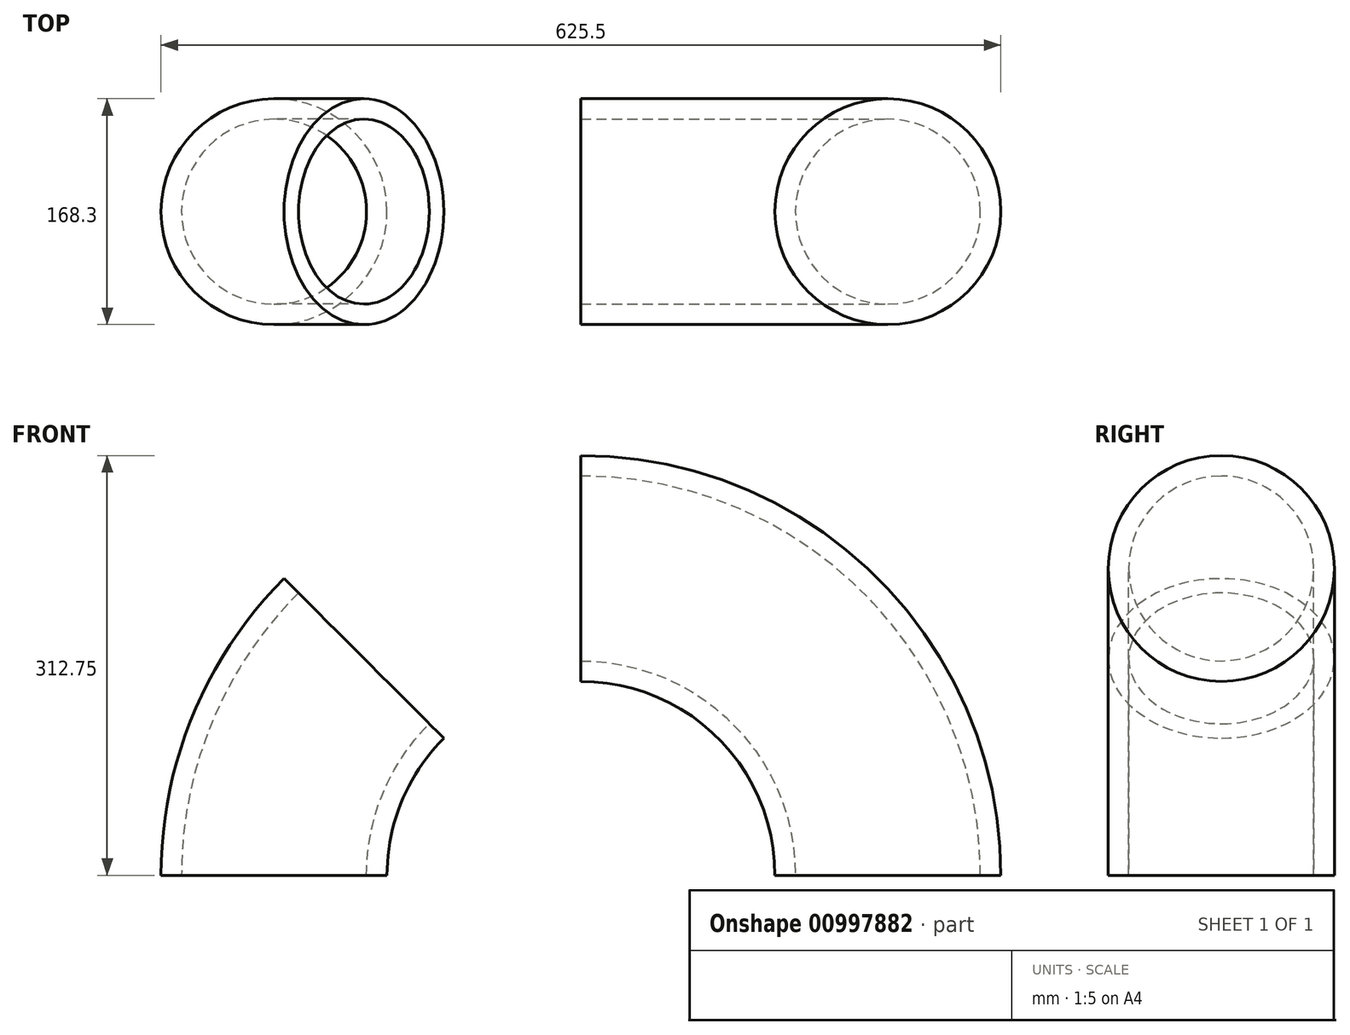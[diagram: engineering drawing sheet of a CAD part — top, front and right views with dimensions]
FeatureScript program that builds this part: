
annotation { "Feature Type Name" : "Feature", "Feature Type Description" : "" }
export const myFeature = defineFeature(function(context is Context, id is Id, definition is map)
    precondition{}
    {
        {
            var Q0;
            Q0=qCreatedBy(makeId("Front.planeOp"),FACE);
            var sketch = newSketch(context, id + "F0", { "sketchPlane" : qUnion([Q0])});
            skArc(sketch, "E0", {"start": v(-228.6, 0) * mm, "mid": v(-211.2, 87.48) * mm, "end": v(-161.64, 161.64) * mm});
            skLineSegment(sketch, "E1", {"start": v(-228.6, 0) * mm, "end": v(257.5, 0) * mm, "construction": true});
            skLineSegment(sketch, "E2", {"start": v(-161.64, 161.64) * mm, "end": v(0, 0) * mm, "construction": true});
            skSolve(sketch);
        }
        {
            var Q0;
            Q0=qCreatedBy(makeId("Top.planeOp"),FACE);
            var sketch = newSketch(context, id + "F1", { "sketchPlane" : qUnion([Q0])});
            skPoint(sketch, "E3.0", {"position": v(-228.6, 0) * mm});
            skCircle(sketch, "E4", {"center": v(-228.6, 0) * mm, "radius": 84.15 * mm});
            skCircle(sketch, "E5", {"center": v(-228.6, 0) * mm, "radius": 68.9 * mm});
            skSolve(sketch);
        }
        {
            var Q0;
            Q0=makeQuery(id+"F1.imprint","IMPRINT",FACE,{"disambiguationData":[TD([[makeQuery(id+"F1.imprint","IMPRINT",EDGE,{"derivedFrom":sQuery(id+"F1.wireOp",EDGE,"E4")}),1.0]])]});
            var Q1;
            Q1=sQuery(id+"F0.wireOp",EDGE,"E0");
            sweep(context, id + "F2", {"profiles" : qUnion([Q0]), "path" : qUnion([Q1])});
        }
        {
            var Q0;
            Q0=qCreatedBy(makeId("Front.planeOp"),FACE);
            var sketch = newSketch(context, id + "F3", { "sketchPlane" : qUnion([Q0])});
            skArc(sketch, "E6", {"start": v(228.6, 0) * mm, "mid": v(161.64, 161.64) * mm, "end": v(0, 228.6) * mm});
            skSolve(sketch);
        }
        {
            var Q0;
            Q0=qCreatedBy(makeId("Top.planeOp"),FACE);
            var sketch = newSketch(context, id + "F4", { "sketchPlane" : qUnion([Q0])});
            skPoint(sketch, "E7.0", {"position": v(228.6, 0) * mm});
            skCircle(sketch, "E8", {"center": v(228.6, 0) * mm, "radius": 84.15 * mm});
            skCircle(sketch, "E9", {"center": v(228.6, 0) * mm, "radius": 68.9 * mm});
            skSolve(sketch);
        }
        {
            var Q0;
            Q0=makeQuery(id+"F4.imprint","IMPRINT",FACE,{"disambiguationData":[TD([[makeQuery(id+"F4.imprint","IMPRINT",EDGE,{"derivedFrom":sQuery(id+"F4.wireOp",EDGE,"E8")}),1.0]])]});
            var Q1;
            Q1=sQuery(id+"F3.wireOp",EDGE,"E6");
            sweep(context, id + "F5", {"profiles" : qUnion([Q0]), "path" : qUnion([Q1])});
        }
    });
